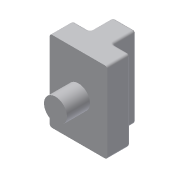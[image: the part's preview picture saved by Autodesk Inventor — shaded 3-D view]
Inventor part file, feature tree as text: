
AUTODESK INVENTOR PART (.ipt)
format: ipt  version: 2014 (Build 180170000, 170)  size: 125,952 bytes
history: native  units: mm
features: extrude x2, sketch x2, fillet x1
ambient origin geometry x8: Origin, YZ Plane, XZ Plane, XY Plane, X Axis, Y Axis, Z Axis, Center Point
bodies: Solid1 (feature_tree)
feature tree (5):
  extrude  "Extrusion1"  Depth=20.0mm
  extrude  "Extrusion2"  Depth=20.0mm
  fillet  "Fillet1"  Radius=70.0mm
  sketch  "Sketch1"  dims[d0=50.0mm d1=20.0mm]
  sketch  "Sketch2"  dims[d2=20.0mm d3=20.0mm d4=70.0mm d5=0.0mm d6=20.0mm d7=20.0mm d8=0.0mm d9=2.0mm d10=2.0mm]
